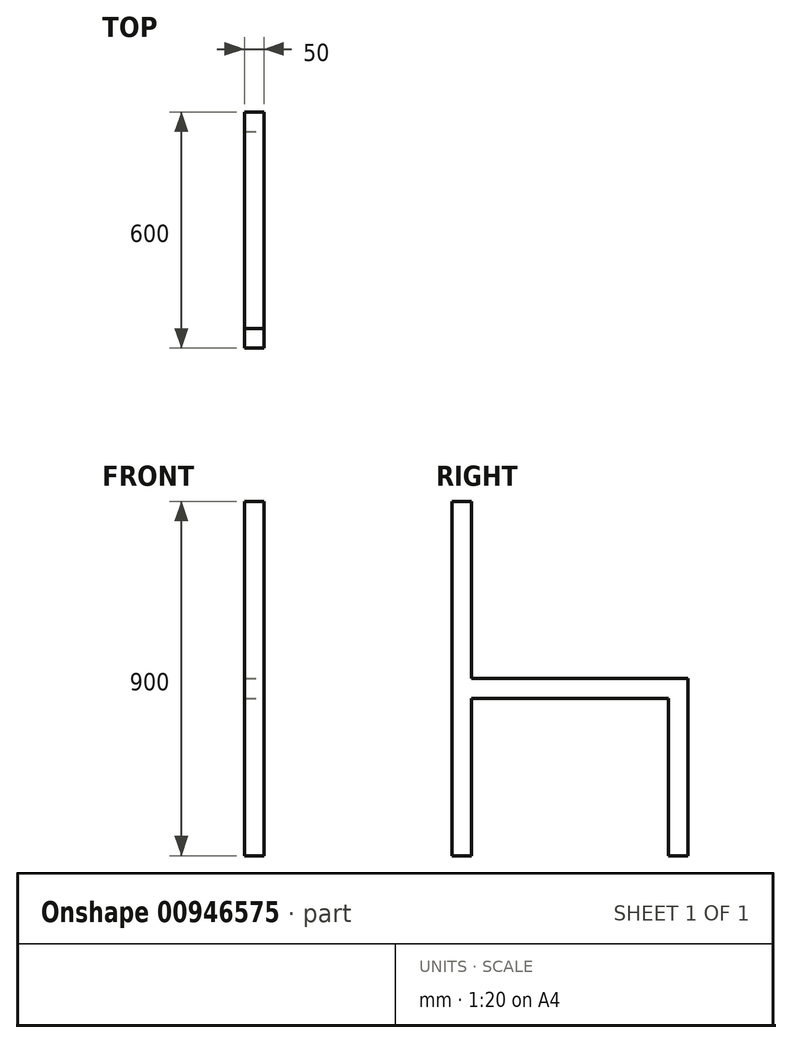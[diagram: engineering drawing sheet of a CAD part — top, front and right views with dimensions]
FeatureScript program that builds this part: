
annotation { "Feature Type Name" : "Feature", "Feature Type Description" : "" }
export const myFeature = defineFeature(function(context is Context, id is Id, definition is map)
    precondition{}
    {
        {
            var Q0;
            Q0=qCreatedBy(makeId("Right.planeOp"),FACE);
            var sketch = newSketch(context, id + "F0", { "sketchPlane" : qUnion([Q0])});
            skLineSegment(sketch, "E0.bottom", {"start": v(-300, 450) * mm, "end": v(300, 450) * mm});
            skLineSegment(sketch, "E0.top", {"start": v(-300, -450) * mm, "end": v(300, -450) * mm});
            skLineSegment(sketch, "E0.left", {"start": v(-300, 450) * mm, "end": v(-300, -450) * mm});
            skLineSegment(sketch, "E0.right", {"start": v(300, 450) * mm, "end": v(300, -450) * mm});
            skSolve(sketch);
        }
        {
            var Q0;
            Q0=makeQuery(id+"F0.imprint","IMPRINT",FACE,{"disambiguationData":[TD([[makeQuery(id+"F0.imprint","IMPRINT",EDGE,{"derivedFrom":sQuery(id+"F0.wireOp",EDGE,"E0.bottom")}),-1.0]])]});
            extrude(context, id + "F1", {"entities" : qUnion([Q0]), "endBound" : BoundingType.SYMMETRIC, "depth" : 50 * mm, "offsetDistance" : 25 * mm});
        }
        {
            var Q0;
            Q0=makeQuery(id+"F1.opExtrude","CAP_FACE",FACE,{"disambiguationData":[OSD([sQuery(id+"F0.wireOp",EDGE,"E0.bottom"),sQuery(id+"F0.wireOp",EDGE,"E0.top"),sQuery(id+"F0.wireOp",EDGE,"E0.left"),sQuery(id+"F0.wireOp",EDGE,"E0.right")])],"isStart":false});
            var sketch = newSketch(context, id + "F2", { "sketchPlane" : qUnion([Q0])});
            skLineSegment(sketch, "E1.bottom", {"start": v(300, 450) * mm, "end": v(-250, 450) * mm});
            skLineSegment(sketch, "E1.top", {"start": v(300, 0) * mm, "end": v(-250, 0) * mm});
            skLineSegment(sketch, "E1.left", {"start": v(300, 450) * mm, "end": v(300, 0) * mm});
            skLineSegment(sketch, "E1.right", {"start": v(-250, 450) * mm, "end": v(-250, 0) * mm});
            skSolve(sketch);
        }
        {
            var Q0;
            Q0=makeQuery(id+"F2.imprint","IMPRINT",FACE,{"disambiguationData":[TD([[makeQuery(id+"F2.imprint","IMPRINT",EDGE,{"derivedFrom":sQuery(id+"F2.wireOp",EDGE,"E1.bottom")}),-1.0]])]});
            extrude(context, id + "F3", {"entities" : qUnion([Q0]), "operationType" : NewBodyOperationType.REMOVE, "endBound" : BoundingType.THROUGH_ALL, "oppositeDirection" : true, "depth" : 25 * mm, "offsetDistance" : 25 * mm});
        }
        {
            var Q0;
            Q0=makeQuery(id+"F1.opExtrude","CAP_FACE",FACE,{"disambiguationData":[OSD([sQuery(id+"F0.wireOp",EDGE,"E0.bottom"),sQuery(id+"F0.wireOp",EDGE,"E0.top"),sQuery(id+"F0.wireOp",EDGE,"E0.left"),sQuery(id+"F0.wireOp",EDGE,"E0.right")])],"isStart":false});
            var sketch = newSketch(context, id + "F4", { "sketchPlane" : qUnion([Q0])});
            skLineSegment(sketch, "E2.bottom", {"start": v(-250, -450) * mm, "end": v(250, -450) * mm});
            skLineSegment(sketch, "E2.top", {"start": v(-250, -50) * mm, "end": v(250, -50) * mm});
            skLineSegment(sketch, "E2.left", {"start": v(-250, -450) * mm, "end": v(-250, -50) * mm});
            skLineSegment(sketch, "E2.right", {"start": v(250, -450) * mm, "end": v(250, -50) * mm});
            skSolve(sketch);
        }
        {
            var Q0;
            Q0=makeQuery(id+"F4.imprint","IMPRINT",FACE,{"disambiguationData":[TD([[makeQuery(id+"F4.imprint","IMPRINT",EDGE,{"derivedFrom":sQuery(id+"F4.wireOp",EDGE,"E2.bottom")}),1.0]])]});
            extrude(context, id + "F5", {"entities" : qUnion([Q0]), "operationType" : NewBodyOperationType.REMOVE, "endBound" : BoundingType.THROUGH_ALL, "oppositeDirection" : true, "depth" : 25 * mm, "offsetDistance" : 25 * mm});
        }
    });
